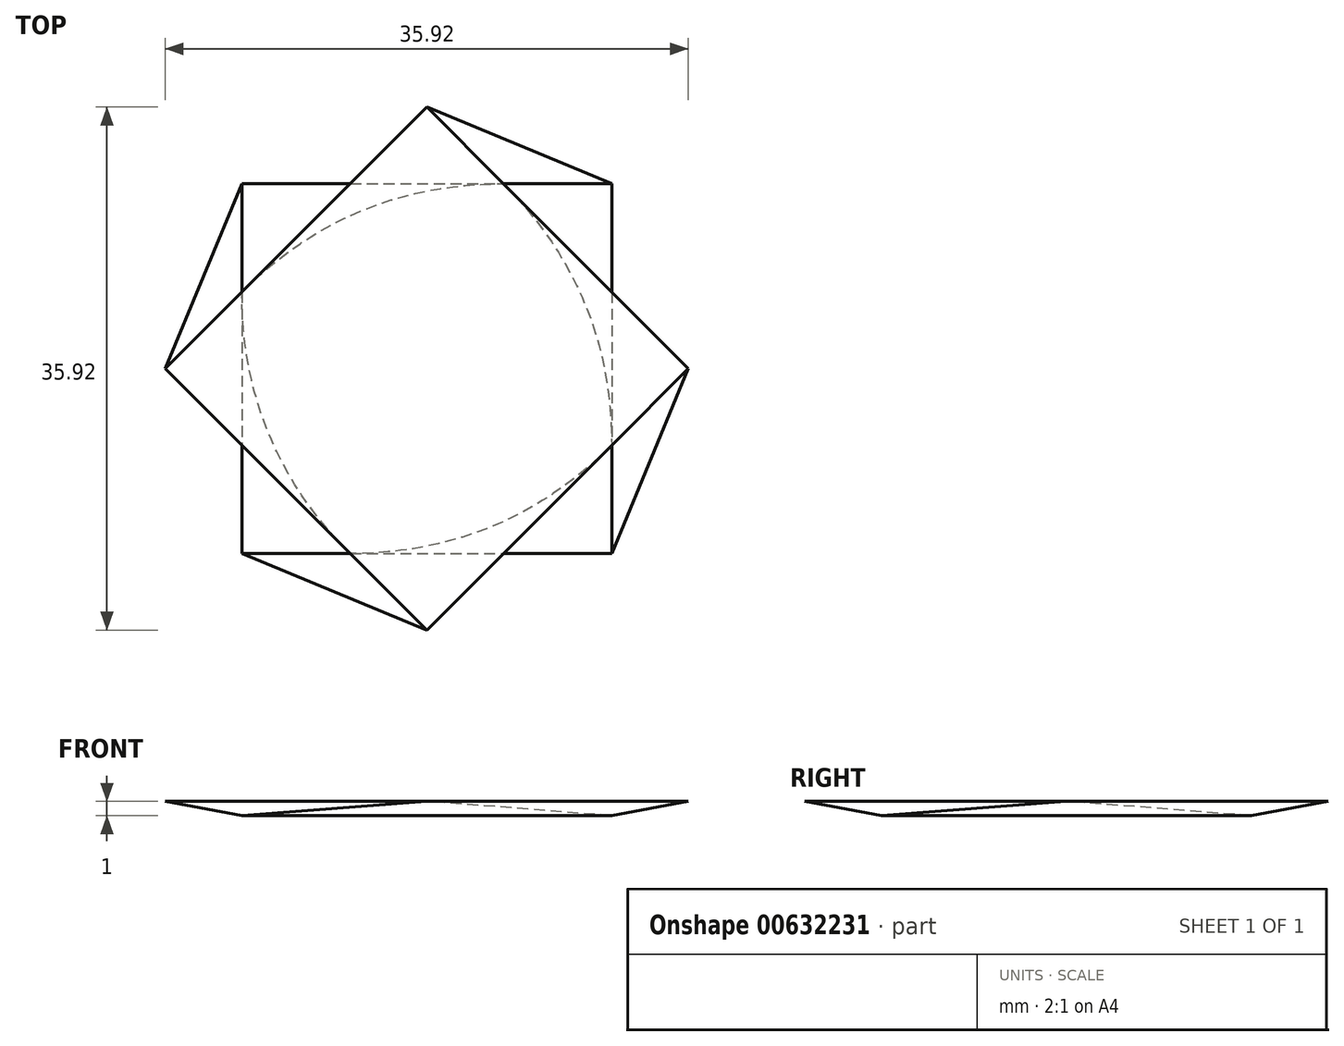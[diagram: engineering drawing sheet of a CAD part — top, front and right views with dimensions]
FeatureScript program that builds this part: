
annotation { "Feature Type Name" : "Feature", "Feature Type Description" : "" }
export const myFeature = defineFeature(function(context is Context, id is Id, definition is map)
    precondition{}
    {
        {
            assignVariable(context, id + "F0", {"name" : "x", "anyValue" : 1});
        }
        {
            var Q0;
            Q0=qCreatedBy(makeId("Top.planeOp"),FACE);
            var sketch = newSketch(context, id + "F1", { "sketchPlane" : qUnion([Q0])});
            skLineSegment(sketch, "E0.bottom", {"start": v(-12.7, 12.7) * mm, "end": v(12.7, 12.7) * mm});
            skLineSegment(sketch, "E0.top", {"start": v(-12.7, -12.7) * mm, "end": v(12.7, -12.7) * mm});
            skLineSegment(sketch, "E0.left", {"start": v(-12.7, 12.7) * mm, "end": v(-12.7, -12.7) * mm});
            skLineSegment(sketch, "E0.right", {"start": v(12.7, 12.7) * mm, "end": v(12.7, -12.7) * mm});
            skSolve(sketch);
        }
        {
            var Q0;
            Q0=qCreatedBy(makeId("Top.planeOp"),FACE);
            cPlane(context, id + "F2", {"entities" : qUnion([Q0]), "cplaneType" : CPlaneType.OFFSET, "offset" : (getVariable(context, 'x')) * mm, "width" : 152.4 * mm, "height" : 152.4 * mm});
        }
        {
            var Q0;
            Q0=qCreatedBy(id+"F2.planeOp",FACE);
            var sketch = newSketch(context, id + "F3", { "sketchPlane" : qUnion([Q0])});
            skLineSegment(sketch, "E1", {"start": v(0, 17.96) * mm, "end": v(-17.96, 0) * mm});
            skLineSegment(sketch, "E2", {"start": v(-17.96, 0) * mm, "end": v(0, -17.96) * mm});
            skLineSegment(sketch, "E3", {"start": v(0, -17.96) * mm, "end": v(17.96, 0) * mm});
            skLineSegment(sketch, "E4", {"start": v(17.96, 0) * mm, "end": v(0, 17.96) * mm});
            skSolve(sketch);
        }
        {
            var Q0;
            Q0=makeQuery(id+"F1.imprint","IMPRINT",FACE,{"disambiguationData":[TD([[makeQuery(id+"F1.imprint","IMPRINT",EDGE,{"derivedFrom":sQuery(id+"F1.wireOp",EDGE,"E0.bottom")}),-1.0]])]});
            var Q1;
            Q1=makeQuery(id+"F3.imprint","IMPRINT",FACE,{"disambiguationData":[TD([[makeQuery(id+"F3.imprint","IMPRINT",EDGE,{"derivedFrom":sQuery(id+"F3.wireOp",EDGE,"E1")}),1.0]])]});
            loft(context, id + "F4", {"sheetProfilesArray" : [{ "sheetProfileEntities" : qUnion([Q0]) }, { "sheetProfileEntities" : qUnion([Q1]) }]});
        }
    });
